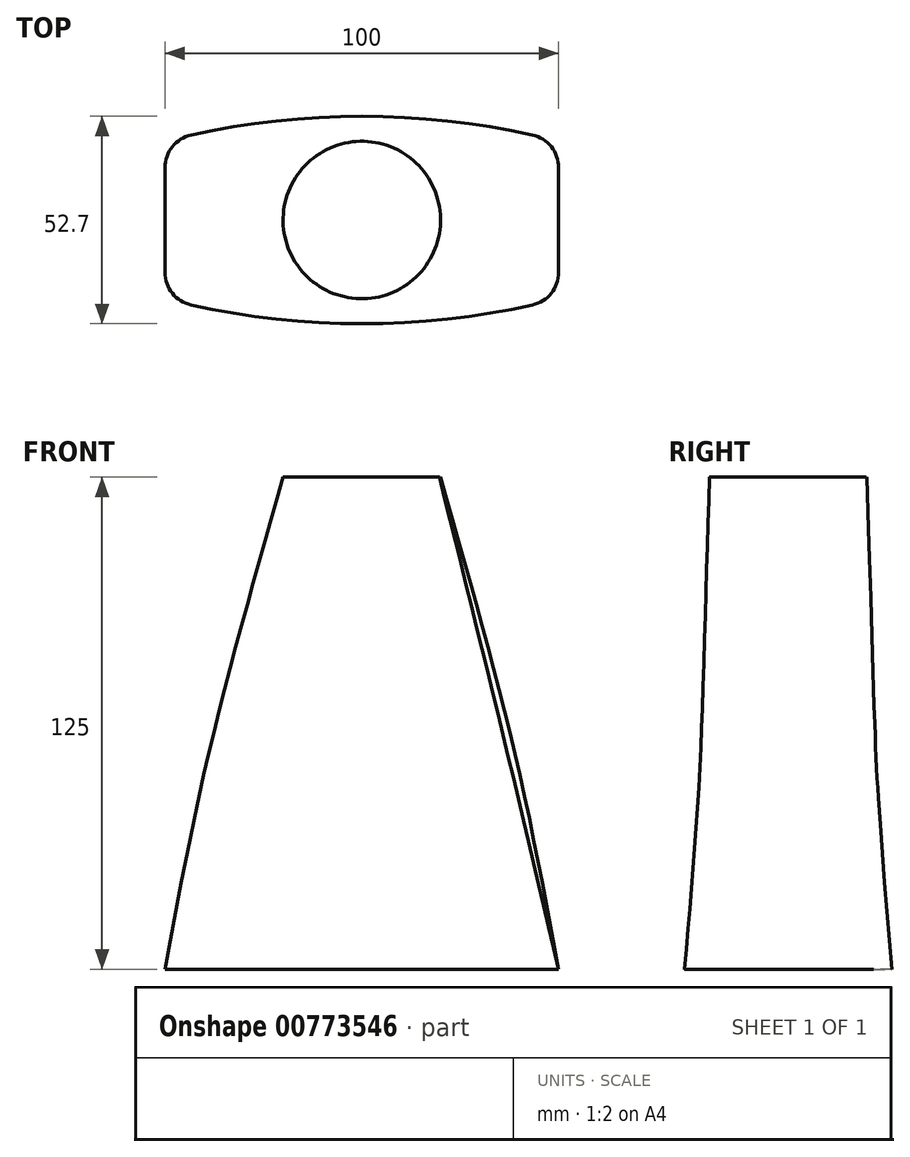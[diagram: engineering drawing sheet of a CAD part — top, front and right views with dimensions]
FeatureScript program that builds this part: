
annotation { "Feature Type Name" : "Feature", "Feature Type Description" : "" }
export const myFeature = defineFeature(function(context is Context, id is Id, definition is map)
    precondition{}
    {
        {
            var Q0;
            Q0=qCreatedBy(makeId("Top.planeOp"),FACE);
            var sketch = newSketch(context, id + "F0", { "sketchPlane" : qUnion([Q0])});
            skLineSegment(sketch, "E0.bottom", {"start": v(50, -20) * mm, "end": v(-50, -20) * mm, "construction": true});
            skLineSegment(sketch, "E0.top", {"start": v(50, 20) * mm, "end": v(-50, 20) * mm, "construction": true});
            skLineSegment(sketch, "E0.left", {"start": v(50, -13.3) * mm, "end": v(50, 13.3) * mm});
            skLineSegment(sketch, "E0.right", {"start": v(-50, -13.3) * mm, "end": v(-50, 13.3) * mm});
            skPoint(sketch, "E0.middle", {"position": v(0, 0) * mm});
            skArc(sketch, "E1", {"start": v(43.34, 21.6) * mm, "mid": v(0, 26.35) * mm, "end": v(-43.34, 21.6) * mm});
            skArc(sketch, "E2", {"start": v(-43.34, -21.6) * mm, "mid": v(0, -26.35) * mm, "end": v(43.34, -21.6) * mm});
            skPoint(sketch, "E3.visualSharp", {"position": v(-50, 20) * mm});
            skArc(sketch, "E3.filletArc", {"start": v(-43.34, 21.6) * mm, "mid": v(-48.13, 18.62) * mm, "end": v(-50, 13.3) * mm});
            skPoint(sketch, "E4.visualSharp", {"position": v(-50, -20) * mm});
            skArc(sketch, "E4.filletArc", {"start": v(-50, -13.3) * mm, "mid": v(-48.13, -18.62) * mm, "end": v(-43.34, -21.6) * mm});
            skPoint(sketch, "E5.visualSharp", {"position": v(50, -20) * mm});
            skArc(sketch, "E5.filletArc", {"start": v(43.34, -21.6) * mm, "mid": v(48.13, -18.62) * mm, "end": v(50, -13.3) * mm});
            skPoint(sketch, "E6.visualSharp", {"position": v(50, 20) * mm});
            skArc(sketch, "E6.filletArc", {"start": v(50, 13.3) * mm, "mid": v(48.13, 18.62) * mm, "end": v(43.34, 21.6) * mm});
            skSolve(sketch);
        }
        {
            var Q0;
            Q0=qCreatedBy(makeId("Top.planeOp"),FACE);
            cPlane(context, id + "F1", {"entities" : qUnion([Q0]), "cplaneType" : CPlaneType.OFFSET, "offset" : 50 * mm, "width" : 150 * mm, "height" : 150 * mm});
        }
        {
            var Q0;
            Q0=qCreatedBy(id+"F1.planeOp",FACE);
            var sketch = newSketch(context, id + "F2", { "sketchPlane" : qUnion([Q0])});
            skEllipse(sketch, "E7", {"center": v(0, 0) * mm, "majorRadius": 40 * mm, "minorRadius": 22.5 * mm, "majorAxis": v(-1, 0)});
            skSolve(sketch);
        }
        {
            var Q0;
            Q0=qCreatedBy(makeId("Top.planeOp"),FACE);
            cPlane(context, id + "F3", {"entities" : qUnion([Q0]), "cplaneType" : CPlaneType.OFFSET, "offset" : 125 * mm, "width" : 150 * mm, "height" : 150 * mm});
        }
        {
            var Q0;
            Q0=qCreatedBy(id+"F3.planeOp",FACE);
            var sketch = newSketch(context, id + "F4", { "sketchPlane" : qUnion([Q0])});
            skCircle(sketch, "E8", {"center": v(0, 0) * mm, "radius": 20 * mm});
            skSolve(sketch);
        }
        {
            var Q0;
            Q0=qSketchRegion(id+"F0",true);
            var Q1;
            Q1=qSketchRegion(id+"F2",true);
            var Q2;
            Q2=qSketchRegion(id+"F4",true);
            loft(context, id + "F5", {"sheetProfilesArray" : [{ "sheetProfileEntities" : qUnion([Q0]) }, { "sheetProfileEntities" : qUnion([Q1]) }, { "sheetProfileEntities" : qUnion([Q2]) }]});
        }
    });
